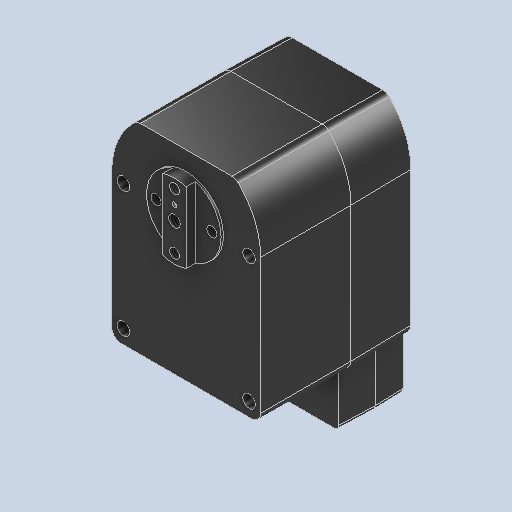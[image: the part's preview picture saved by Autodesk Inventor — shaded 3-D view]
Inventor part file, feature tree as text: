
AUTODESK INVENTOR PART (.ipt)
format: ipt  version: 2024.2 (Build 282272000, 272)  size: 322,048 bytes
history: native  units: mm
features: chamfer x9, hole x7, extrude x6, fillet x2
ambient origin geometry x8: Origin, YZ Plane, XZ Plane, XY Plane, X Axis, Y Axis, Z Axis, Center Point
bodies: Solid1 (feature_tree)
feature tree (24):
  extrude  "Extrusion1"  Depth=16.0mm
  extrude  "Extrusion2"  Depth=16.0mm
  extrude  "Extrusion3"  Depth=43.0mm
  extrude  "Extrusion4"  Depth=9.5mm
  extrude  "Extrusion5"  Depth=32.0mm
  extrude  "Extrusion6"  Depth=28.8mm
  hole  "Hole1"  [1 undecoded]
  hole  "Hole2"  [1 undecoded]
  hole  "Hole3"  [1 undecoded]
  hole  "Hole4"  [1 undecoded]
  hole  "Hole5"  [1 undecoded]
  hole  "Hole6"  [1 undecoded]
  hole  "Hole7"  [1 undecoded]
  chamfer  "Chamfer1"  Distance=12.0mm
  chamfer  "Chamfer2"  Distance=32.5mm
  chamfer  "Chamfer3"  Distance=14.0mm
  chamfer  "Chamfer4"  Distance=0.2mm
  chamfer  "Chamfer5"  Distance=0.5mm
  chamfer  "Chamfer6"  Distance=2.0mm
  chamfer  "Chamfer7"  Distance=0.174533mm
  chamfer  "Chamfer8"  Distance=0.174533mm
  chamfer  "Chamfer9"  Distance=0.174533mm
  fillet  "Fillet1"  Radius=0.174533mm
  fillet  "Fillet2"  Radius=0.174533mm
note: 7 required parameter values undecoded (feature->parameter linkage not recoverable at this tier; creation-order binding heuristic only, values carry confidence <= 0.55)
